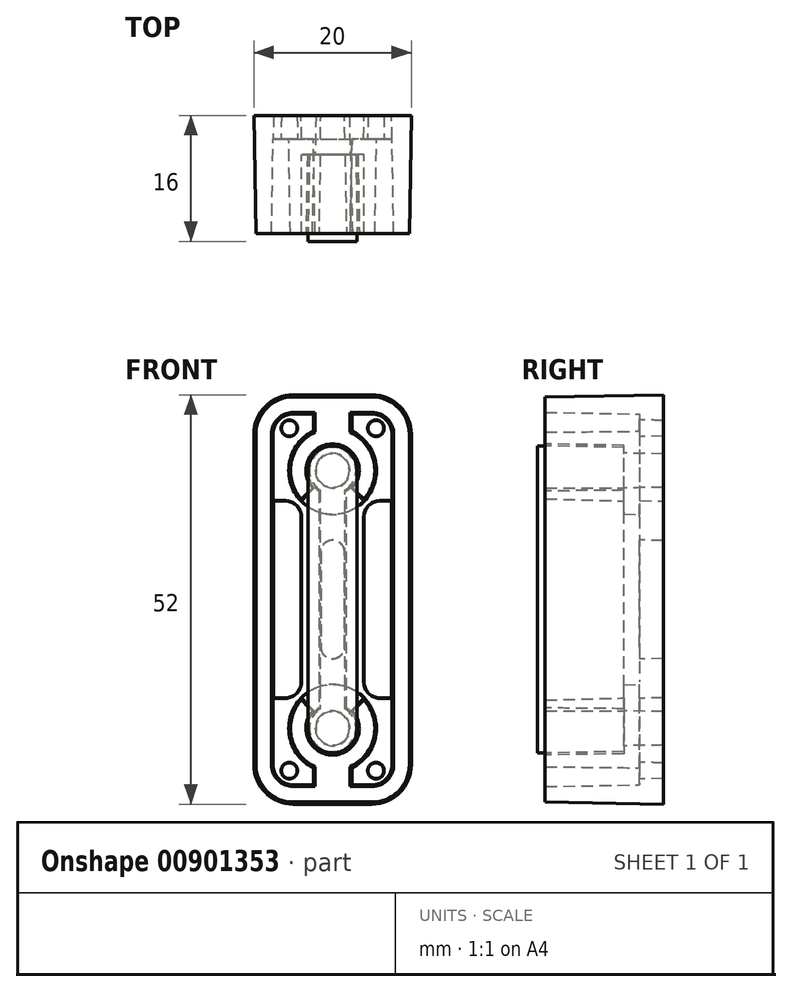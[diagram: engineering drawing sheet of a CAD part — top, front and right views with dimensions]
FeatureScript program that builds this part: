
annotation { "Feature Type Name" : "Feature", "Feature Type Description" : "" }
export const myFeature = defineFeature(function(context is Context, id is Id, definition is map)
    precondition{}
    {
        {
            var Q0;
            Q0=qCreatedBy(makeId("Front.planeOp"),FACE);
            var sketch = newSketch(context, id + "F0", { "sketchPlane" : qUnion([Q0])});
            skLineSegment(sketch, "E0", {"start": v(0, 0) * mm, "end": v(0, 26) * mm, "construction": true});
            skLineSegment(sketch, "E1", {"start": v(0, 0) * mm, "end": v(10, 0) * mm, "construction": true});
            skLineSegment(sketch, "E2.bottom", {"start": v(-5, -26) * mm, "end": v(5, -26) * mm});
            skLineSegment(sketch, "E2.top", {"start": v(-5, 26) * mm, "end": v(5, 26) * mm});
            skLineSegment(sketch, "E2.left", {"start": v(-10, -21) * mm, "end": v(-10, 21) * mm});
            skLineSegment(sketch, "E2.right", {"start": v(10, -21) * mm, "end": v(10, 21) * mm});
            skPoint(sketch, "E3.visualSharp", {"position": v(-10, 26) * mm});
            skArc(sketch, "E3.filletArc", {"start": v(-5, 26) * mm, "mid": v(-8.54, 24.54) * mm, "end": v(-10, 21) * mm});
            skPoint(sketch, "E4.visualSharp", {"position": v(10, 26) * mm});
            skArc(sketch, "E4.filletArc", {"start": v(10, 21) * mm, "mid": v(8.54, 24.54) * mm, "end": v(5, 26) * mm});
            skPoint(sketch, "E5.visualSharp", {"position": v(10, -26) * mm});
            skArc(sketch, "E5.filletArc", {"start": v(5, -26) * mm, "mid": v(8.54, -24.54) * mm, "end": v(10, -21) * mm});
            skPoint(sketch, "E6.visualSharp", {"position": v(-10, -26) * mm});
            skArc(sketch, "E6.filletArc", {"start": v(-10, -21) * mm, "mid": v(-8.54, -24.54) * mm, "end": v(-5, -26) * mm});
            skLineSegment(sketch, "E7.0", {"start": v(-5, 23.5) * mm, "end": v(-2.5, 23.5) * mm});
            skArc(sketch, "E7.1", {"start": v(7.5, 21) * mm, "mid": v(6.77, 22.77) * mm, "end": v(5, 23.5) * mm});
            skArc(sketch, "E7.2", {"start": v(-5, 23.5) * mm, "mid": v(-6.77, 22.77) * mm, "end": v(-7.5, 21) * mm});
            skLineSegment(sketch, "E7.3", {"start": v(7.5, -21) * mm, "end": v(7.5, 21) * mm});
            skLineSegment(sketch, "E7.4", {"start": v(-7.5, -21) * mm, "end": v(-7.5, 21) * mm});
            skArc(sketch, "E7.5", {"start": v(-7.5, -21) * mm, "mid": v(-6.77, -22.77) * mm, "end": v(-5, -23.5) * mm});
            skLineSegment(sketch, "E7.6", {"start": v(-5, -23.5) * mm, "end": v(-2.5, -23.5) * mm});
            skArc(sketch, "E7.7", {"start": v(5, -23.5) * mm, "mid": v(6.77, -22.77) * mm, "end": v(7.5, -21) * mm});
            skArc(sketch, "E8", {"start": v(2.2, 14.17) * mm, "mid": v(0, 19.5) * mm, "end": v(-2.2, 14.17) * mm});
            skArc(sketch, "E9", {"start": v(-2.5, 21.41) * mm, "mid": v(-5.55, 17.28) * mm, "end": v(-3.98, 12.4) * mm});
            skLineSegment(sketch, "E10", {"start": v(-2.5, 23.5) * mm, "end": v(-2.5, 21.41) * mm});
            skLineSegment(sketch, "E11.MirrorCS", {"start": v(2.5, 23.5) * mm, "end": v(2.5, 21.41) * mm});
            skLineSegment(sketch, "E12", {"start": v(0, 16.37) * mm, "end": v(-3.98, 12.4) * mm, "construction": true});
            skLineSegment(sketch, "E13", {"start": v(-3.98, 12.4) * mm, "end": v(-2.2, 14.17) * mm});
            skLineSegment(sketch, "E14.MirrorCS", {"start": v(3.98, 12.4) * mm, "end": v(2.2, 14.17) * mm});
            skArc(sketch, "E15.trimOffspring", {"start": v(3.98, 12.4) * mm, "mid": v(5.55, 17.28) * mm, "end": v(2.5, 21.41) * mm});
            skLineSegment(sketch, "E16.trimOffspring", {"start": v(2.5, 23.5) * mm, "end": v(5, 23.5) * mm});
            skLineSegment(sketch, "E17.MirrorCS", {"start": v(-3.98, -12.4) * mm, "end": v(-2.2, -14.17) * mm});
            skLineSegment(sketch, "E18.MirrorCS", {"start": v(3.98, -12.4) * mm, "end": v(2.2, -14.17) * mm});
            skArc(sketch, "E19.MirrorCS", {"start": v(2.2, -14.17) * mm, "mid": v(0, -19.5) * mm, "end": v(-2.2, -14.17) * mm});
            skArc(sketch, "E20.MirrorCS", {"start": v(3.98, -12.4) * mm, "mid": v(5.55, -17.28) * mm, "end": v(2.5, -21.41) * mm});
            skArc(sketch, "E21.MirrorCS", {"start": v(-2.5, -21.41) * mm, "mid": v(-5.55, -17.28) * mm, "end": v(-3.98, -12.4) * mm});
            skLineSegment(sketch, "E22.MirrorCS", {"start": v(-2.5, -23.5) * mm, "end": v(-2.5, -21.41) * mm});
            skLineSegment(sketch, "E23.MirrorCS", {"start": v(2.5, -23.5) * mm, "end": v(2.5, -21.41) * mm});
            skLineSegment(sketch, "E24.trimOffspring", {"start": v(2.5, -23.5) * mm, "end": v(5, -23.5) * mm});
            skSolve(sketch);
        }
        {
            var Q0;
            Q0=qSketchRegion(id+"F0",true);
            extrude(context, id + "F1", {"entities" : qUnion([Q0]), "depth" : 15 * mm, "offsetDistance" : 25 * mm, "hasDraft" : true, "draftAngle" : 1 * degree, "draftPullDirection" : true});
        }
        {
            var Q0;
            Q0=makeQuery(id+"F1.opExtrude","CAP_FACE",FACE,{"disambiguationData":[OSD([sQuery(id+"F0.wireOp",EDGE,"E2.bottom"),sQuery(id+"F0.wireOp",EDGE,"E2.top"),sQuery(id+"F0.wireOp",EDGE,"E2.left"),sQuery(id+"F0.wireOp",EDGE,"E2.right"),sQuery(id+"F0.wireOp",EDGE,"E3.filletArc"),sQuery(id+"F0.wireOp",EDGE,"E4.filletArc"),sQuery(id+"F0.wireOp",EDGE,"E5.filletArc"),sQuery(id+"F0.wireOp",EDGE,"E6.filletArc"),sQuery(id+"F0.wireOp",EDGE,"IJIhQCWJ-vp5b-zzRw-YyAL-ax2AYMN4Gx5I"),sQuery(id+"F0.wireOp",EDGE,"dh8WImpI-Tz79-VF2Q-ETp0-wnzrXUpZCEhC"),sQuery(id+"F0.wireOp",EDGE,"0e7b83d3-1617-4692-a56a-0df3715140b80.MirrorCS"),sQuery(id+"F0.wireOp",EDGE,"63012ba2-617b-48f9-b086-6f9d92fcfca3.0"),sQuery(id+"F0.wireOp",EDGE,"63012ba2-617b-48f9-b086-6f9d92fcfca3.1"),sQuery(id+"F0.wireOp",EDGE,"63012ba2-617b-48f9-b086-6f9d92fcfca3.2"),sQuery(id+"F0.wireOp",EDGE,"63012ba2-617b-48f9-b086-6f9d92fcfca3.3"),sQuery(id+"F0.wireOp",EDGE,"63012ba2-617b-48f9-b086-6f9d92fcfca3.4"),sQuery(id+"F0.wireOp",EDGE,"63012ba2-617b-48f9-b086-6f9d92fcfca3.5"),sQuery(id+"F0.wireOp",EDGE,"63012ba2-617b-48f9-b086-6f9d92fcfca3.6"),sQuery(id+"F0.wireOp",EDGE,"63012ba2-617b-48f9-b086-6f9d92fcfca3.7"),sQuery(id+"F0.wireOp",EDGE,"8ypiQ47V-67Ep-hSZd-vUGe-sPArIVzfRg9r"),sQuery(id+"F0.wireOp",EDGE,"db96d830-14f2-44ef-9f1c-8a25ea6042630.MirrorCS"),sQuery(id+"F0.wireOp",EDGE,"166b1ac4-9fa9-4f32-b77b-16c1f139f97e.trimOffspring"),sQuery(id+"F0.wireOp",EDGE,"2ea4436b-71ed-4dd2-808e-c51e6bdfdb0d.trimOffspring"),sQuery(id+"F0.wireOp",EDGE,"f16e5e95-2546-4fa4-a395-2924a5706e5d.trimOffspring"),sQuery(id+"F0.wireOp",EDGE,"b140966a-7433-431a-b5f9-24e567881923.trimOffspring"),sQuery(id+"F0.wireOp",EDGE,"92f5dfcb-e6f0-4d8e-a4dd-98843e38dc0c.0"),sQuery(id+"F0.wireOp",EDGE,"e4d454ed-89ad-4555-8113-6ffb95010345.trimOffspring"),sQuery(id+"F0.wireOp",EDGE,"501d84ee-e220-4e0b-91ec-5823b552a726.trimOffspring"),sQuery(id+"F0.wireOp",EDGE,"22b5fe90-0e15-4b88-bf77-c0b40cca12cc.trimOffspring"),sQuery(id+"F0.wireOp",EDGE,"23a1b8e1-ace7-4838-b7cc-06f11be78a04.trimOffspring"),sQuery(id+"F0.wireOp",EDGE,"484fa764-ed8e-4453-83f1-a5549a87edd0.trimOffspring"),sQuery(id+"F0.wireOp",EDGE,"704c6e2b-e5a0-4266-ac80-0e0644573a2d.trimOffspring"),sQuery(id+"F0.wireOp",EDGE,"3ff7fe7c-f265-459f-816c-150d40e8648d.trimOffspring"),sQuery(id+"F0.wireOp",EDGE,"bc8dae16-3626-45bc-94f4-57fc1cf7c8cc.filletArc"),sQuery(id+"F0.wireOp",EDGE,"3be0ad83-c638-4309-acda-31639ae874aa.filletArc"),sQuery(id+"F0.wireOp",EDGE,"9c4106e4-e133-4278-b6d4-2dd83974d82b.filletArc"),sQuery(id+"F0.wireOp",EDGE,"51c34a04-a3f6-4a7f-b2ea-3c33f7a80b13.filletArc"),sQuery(id+"F0.wireOp",EDGE,"15e56de6-45aa-4f2f-9f74-d961533e7756.filletArc"),sQuery(id+"F0.wireOp",EDGE,"7f41f25c-c827-4c96-81fa-12fbfe7cb040.filletArc"),sQuery(id+"F0.wireOp",EDGE,"358b29fd-b0bf-40a4-8dc7-75964a047a13.filletArc"),sQuery(id+"F0.wireOp",EDGE,"3f94c72b-eaf8-460e-ae89-1328a0c77947.filletArc"),sQuery(id+"F0.wireOp",EDGE,"28302d16-46e8-4e90-b000-bc3d5d1e7841.filletArc"),sQuery(id+"F0.wireOp",EDGE,"92f77ba2-103b-450e-a273-c03898c0b766.filletArc"),sQuery(id+"F0.wireOp",EDGE,"54d4babc-1001-4ab9-a95e-d1a6663917fc.filletArc"),sQuery(id+"F0.wireOp",EDGE,"99b7f777-bdf4-4760-85df-7bfb9edbce3f.filletArc"),sQuery(id+"F0.wireOp",EDGE,"65ccd1a2-0b74-4b36-a3b8-403cce2e56b0.filletArc"),sQuery(id+"F0.wireOp",EDGE,"db3c6368-bc13-4602-834c-323b036d4deb.filletArc"),sQuery(id+"F0.wireOp",EDGE,"3f13f4ab-db91-420c-805e-83e3af0d3dc1.filletArc"),sQuery(id+"F0.wireOp",EDGE,"402289e9-b3ab-49cc-a322-b51cc4187130.filletArc")])],"isStart":true});
            var sketch = newSketch(context, id + "F2", { "sketchPlane" : qUnion([Q0])});
            skLineSegment(sketch, "E25", {"start": v(0, 0) * mm, "end": v(10, 0) * mm, "construction": true});
            skLineSegment(sketch, "E26", {"start": v(0, 0) * mm, "end": v(0, 31) * mm, "construction": true});
            skLineSegment(sketch, "E27.bottom", {"start": v(-5, 26) * mm, "end": v(5, 26) * mm});
            skLineSegment(sketch, "E27.left", {"start": v(-10, 21) * mm, "end": v(-10, -21) * mm});
            skLineSegment(sketch, "E27.right", {"start": v(10, 21) * mm, "end": v(10, -21) * mm});
            skLineSegment(sketch, "E28", {"start": v(0, 0) * mm, "end": v(0, -31) * mm, "construction": true});
            skLineSegment(sketch, "E29", {"start": v(0, 0) * mm, "end": v(-10, 0) * mm, "construction": true});
            skLineSegment(sketch, "E30", {"start": v(5, -26) * mm, "end": v(-5, -26) * mm});
            skLineSegment(sketch, "E31.bottom", {"start": v(7.5, 12.5) * mm, "end": v(6, 12.5) * mm});
            skLineSegment(sketch, "E31.top", {"start": v(7.5, -12.5) * mm, "end": v(6, -12.5) * mm});
            skLineSegment(sketch, "E31.left", {"start": v(7.5, 12.5) * mm, "end": v(7.5, -12.5) * mm});
            skLineSegment(sketch, "E31.right", {"start": v(4, 10.5) * mm, "end": v(4, -10.5) * mm});
            skLineSegment(sketch, "E32.MirrorCS", {"start": v(-7.5, 12.5) * mm, "end": v(-7.5, -12.5) * mm});
            skLineSegment(sketch, "E33.MirrorCS", {"start": v(-7.5, 12.5) * mm, "end": v(-6, 12.5) * mm});
            skLineSegment(sketch, "E34.MirrorCS", {"start": v(-4, 10.5) * mm, "end": v(-4, -10.5) * mm});
            skLineSegment(sketch, "E35.MirrorCS", {"start": v(-7.5, -12.5) * mm, "end": v(-6, -12.5) * mm});
            skPoint(sketch, "E36.visualSharp", {"position": v(10, 26) * mm});
            skArc(sketch, "E36.filletArc", {"start": v(10, 21) * mm, "mid": v(8.54, 24.54) * mm, "end": v(5, 26) * mm});
            skPoint(sketch, "E37.visualSharp", {"position": v(-10, 26) * mm});
            skArc(sketch, "E37.filletArc", {"start": v(-5, 26) * mm, "mid": v(-8.54, 24.54) * mm, "end": v(-10, 21) * mm});
            skPoint(sketch, "E38.visualSharp", {"position": v(-10, -26) * mm});
            skArc(sketch, "E38.filletArc", {"start": v(-10, -21) * mm, "mid": v(-8.54, -24.54) * mm, "end": v(-5, -26) * mm});
            skPoint(sketch, "E39.visualSharp", {"position": v(10, -26) * mm});
            skArc(sketch, "E39.filletArc", {"start": v(5, -26) * mm, "mid": v(8.54, -24.54) * mm, "end": v(10, -21) * mm});
            skCircle(sketch, "E40", {"center": v(-5.5, 21.75) * mm, "radius": 1 * mm});
            skCircle(sketch, "E41.MirrorC", {"center": v(5.5, 21.75) * mm, "radius": 1 * mm});
            skCircle(sketch, "E42.MirrorC", {"center": v(-5.5, -21.75) * mm, "radius": 1 * mm});
            skCircle(sketch, "E43.MirrorC", {"center": v(5.5, -21.75) * mm, "radius": 1 * mm});
            skPoint(sketch, "E44.visualSharp", {"position": v(4, 12.5) * mm});
            skArc(sketch, "E44.filletArc", {"start": v(6, 12.5) * mm, "mid": v(4.59, 11.91) * mm, "end": v(4, 10.5) * mm});
            skPoint(sketch, "E45.visualSharp", {"position": v(-4, 12.5) * mm});
            skArc(sketch, "E45.filletArc", {"start": v(-4, 10.5) * mm, "mid": v(-4.59, 11.91) * mm, "end": v(-6, 12.5) * mm});
            skPoint(sketch, "E46.visualSharp", {"position": v(4, -12.5) * mm});
            skArc(sketch, "E46.filletArc", {"start": v(4, -10.5) * mm, "mid": v(4.59, -11.91) * mm, "end": v(6, -12.5) * mm});
            skPoint(sketch, "E47.visualSharp", {"position": v(-4, -12.5) * mm});
            skArc(sketch, "E47.filletArc", {"start": v(-6, -12.5) * mm, "mid": v(-4.59, -11.91) * mm, "end": v(-4, -10.5) * mm});
            skLineSegment(sketch, "E48", {"start": v(-1.5, 6) * mm, "end": v(-1.5, -6) * mm});
            skLineSegment(sketch, "E49", {"start": v(-1.5, -6) * mm, "end": v(1.5, -6) * mm, "construction": true});
            skLineSegment(sketch, "E50.MirrorCS", {"start": v(-1.5, 6) * mm, "end": v(1.5, 6) * mm, "construction": true});
            skLineSegment(sketch, "E51.MirrorCS", {"start": v(1.5, 6) * mm, "end": v(1.5, -6) * mm});
            skArc(sketch, "E52", {"start": v(1.5, 6) * mm, "mid": v(0, 7.5) * mm, "end": v(-1.5, 6) * mm});
            skArc(sketch, "E53", {"start": v(-1.5, -6) * mm, "mid": v(0, -7.5) * mm, "end": v(1.5, -6) * mm});
            skCircle(sketch, "E54", {"center": v(0, 16.37) * mm, "radius": 2.12 * mm});
            skCircle(sketch, "E55", {"center": v(0, -16.37) * mm, "radius": 2.12 * mm});
            skSolve(sketch);
        }
        {
            var Q0;
            Q0=qSketchRegion(id+"F2",true);
            extrude(context, id + "F3", {"entities" : qUnion([Q0]), "operationType" : NewBodyOperationType.ADD, "oppositeDirection" : true, "depth" : 3 * mm, "offsetDistance" : 25 * mm, "hasDraft" : true, "draftAngle" : 1 * degree, "draftPullDirection" : true});
        }
        {
            var Q0;
            Q0=qCreatedBy(makeId("Front.planeOp"),FACE);
            var sketch = newSketch(context, id + "F4", { "sketchPlane" : qUnion([Q0])});
            skPoint(sketch, "E56.0", {"position": v(0, 16.37) * mm});
            skCircle(sketch, "E57", {"center": v(0, 16.37) * mm, "radius": 5.62 * mm});
            skCircle(sketch, "E58.0", {"center": v(0, 16.37) * mm, "radius": 2.12 * mm});
            skLineSegment(sketch, "E59.0", {"start": v(0, 0) * mm, "end": v(10, 0) * mm, "construction": true});
            skCircle(sketch, "E60.MirrorC", {"center": v(0, -16.37) * mm, "radius": 5.62 * mm});
            skCircle(sketch, "E61.MirrorC", {"center": v(0, -16.37) * mm, "radius": 2.12 * mm});
            skSolve(sketch);
        }
        {
            var Q0;
            Q0 = qSketchRegion(id + "F4", true);
            extrude(context, id + "F5", {"entities" : qUnion([Q0]), "operationType" : NewBodyOperationType.ADD, "depth" : 5 * mm, "offsetDistance" : 25 * mm, "hasDraft" : true, "draftAngle" : 1 * degree, "draftPullDirection" : true});
        }
        {
            var Q0;
            Q0=makeQuery(id+"F1.opExtrude","CAP_FACE",FACE,{"disambiguationData":[OSD([sQuery(id+"F0.wireOp",EDGE,"E2.bottom"),sQuery(id+"F0.wireOp",EDGE,"E2.top"),sQuery(id+"F0.wireOp",EDGE,"E2.left"),sQuery(id+"F0.wireOp",EDGE,"E2.right"),sQuery(id+"F0.wireOp",EDGE,"E3.filletArc"),sQuery(id+"F0.wireOp",EDGE,"E4.filletArc"),sQuery(id+"F0.wireOp",EDGE,"E5.filletArc"),sQuery(id+"F0.wireOp",EDGE,"E6.filletArc"),sQuery(id+"F0.wireOp",EDGE,"E7.0"),sQuery(id+"F0.wireOp",EDGE,"E7.1"),sQuery(id+"F0.wireOp",EDGE,"E7.2"),sQuery(id+"F0.wireOp",EDGE,"E7.3"),sQuery(id+"F0.wireOp",EDGE,"E7.4"),sQuery(id+"F0.wireOp",EDGE,"E7.5"),sQuery(id+"F0.wireOp",EDGE,"E7.6"),sQuery(id+"F0.wireOp",EDGE,"E7.7"),sQuery(id+"F0.wireOp",EDGE,"E8"),sQuery(id+"F0.wireOp",EDGE,"E9"),sQuery(id+"F0.wireOp",EDGE,"E10"),sQuery(id+"F0.wireOp",EDGE,"E11.MirrorCS"),sQuery(id+"F0.wireOp",EDGE,"E13"),sQuery(id+"F0.wireOp",EDGE,"E14.MirrorCS"),sQuery(id+"F0.wireOp",EDGE,"E15.trimOffspring"),sQuery(id+"F0.wireOp",EDGE,"E16.trimOffspring"),sQuery(id+"F0.wireOp",EDGE,"E17.MirrorCS"),sQuery(id+"F0.wireOp",EDGE,"E18.MirrorCS"),sQuery(id+"F0.wireOp",EDGE,"E19.MirrorCS"),sQuery(id+"F0.wireOp",EDGE,"E20.MirrorCS"),sQuery(id+"F0.wireOp",EDGE,"E21.MirrorCS"),sQuery(id+"F0.wireOp",EDGE,"E22.MirrorCS"),sQuery(id+"F0.wireOp",EDGE,"E23.MirrorCS"),sQuery(id+"F0.wireOp",EDGE,"E24.trimOffspring")])],"isStart":false});
            cPlane(context, id + "F6", {"entities" : qUnion([Q0]), "cplaneType" : CPlaneType.OFFSET, "offset" : 0 * mm, "width" : 150 * mm, "height" : 150 * mm});
        }
        {
            var Q0;
            Q0=qCreatedBy(id+"F6.planeOp",FACE);
            var sketch = newSketch(context, id + "F7", { "sketchPlane" : qUnion([Q0])});
            skPoint(sketch, "E62.0", {"position": v(0, 16.37) * mm});
            skPoint(sketch, "E63.0", {"position": v(0, -16.37) * mm});
            skLineSegment(sketch, "E64.0", {"start": v(0, 0) * mm, "end": v(0, 26) * mm, "construction": true});
            skLineSegment(sketch, "E65.0", {"start": v(0, 0) * mm, "end": v(10, 0) * mm, "construction": true});
            skArc(sketch, "E66.0", {"start": v(2.2, 14.17) * mm, "mid": v(0, 19.5) * mm, "end": v(-2.2, 14.17) * mm, "construction": true});
            skCircle(sketch, "E67", {"center": v(0, 16.37) * mm, "radius": 3.12 * mm});
            skCircle(sketch, "E68.MirrorC", {"center": v(0, -16.37) * mm, "radius": 3.12 * mm});
            skLineSegment(sketch, "E69", {"start": v(-1.75, 13.79) * mm, "end": v(-1.75, -13.79) * mm});
            skLineSegment(sketch, "E70.MirrorCS", {"start": v(1.75, 13.79) * mm, "end": v(1.75, -13.79) * mm});
            skSolve(sketch);
        }
        {
            var Q0;
            Q0 = qSketchRegion(id + "F7", true);
            extrude(context, id + "F8", {"entities" : qUnion([Q0]), "oppositeDirection" : true, "depth" : 10 * mm, "offsetDistance" : 25 * mm, "hasDraft" : true, "draftAngle" : 1 * degree, "draftPullDirection" : true});
        }
        {
            var Q0;
            Q0=makeQuery(id+"F8.opExtrude","CAP_FACE",FACE,{"disambiguationData":[OSD([sQuery(id+"F7.wireOp",EDGE,"E67"),sQuery(id+"F7.wireOp",EDGE,"E68.MirrorC"),sQuery(id+"F7.wireOp",EDGE,"E69"),sQuery(id+"F7.wireOp",EDGE,"E70.MirrorCS")])],"isStart":true});
            var sketch = newSketch(context, id + "F9", { "sketchPlane" : qUnion([Q0])});
            skLineSegment(sketch, "E71", {"start": v(0, 0) * mm, "end": v(11.84, 0) * mm, "construction": true});
            skLineSegment(sketch, "E72", {"start": v(0, 0) * mm, "end": v(0, 26.78) * mm, "construction": true});
            skPoint(sketch, "E72.endSnap0", {"position": v(0, 19.5) * mm});
            skArc(sketch, "E73.0", {"start": v(3.12, 16.37) * mm, "mid": v(0, 19.5) * mm, "end": v(-3.12, 16.37) * mm});
            skArc(sketch, "E74.0", {"start": v(3.12, -16.37) * mm, "mid": v(0, -19.5) * mm, "end": v(-3.12, -16.37) * mm});
            skLineSegment(sketch, "E75", {"start": v(-3.12, 16.37) * mm, "end": v(-3.12, -16.37) * mm});
            skLineSegment(sketch, "E76", {"start": v(3.12, 16.37) * mm, "end": v(3.13, -16.37) * mm});
            skPoint(sketch, "E77.orphan", {"position": v(-1.75, 13.79) * mm});
            skPoint(sketch, "E78.orphan", {"position": v(1.75, 13.79) * mm});
            skPoint(sketch, "E79.orphan", {"position": v(-1.75, -13.79) * mm});
            skPoint(sketch, "E80.orphan", {"position": v(1.75, -13.79) * mm});
            skSolve(sketch);
        }
        {
            var Q0;
            Q0 = qSketchRegion(id + "F9", true);
            extrude(context, id + "F10", {"entities" : qUnion([Q0]), "operationType" : NewBodyOperationType.ADD, "depth" : 1 * mm, "offsetDistance" : 25 * mm});
        }
    });
